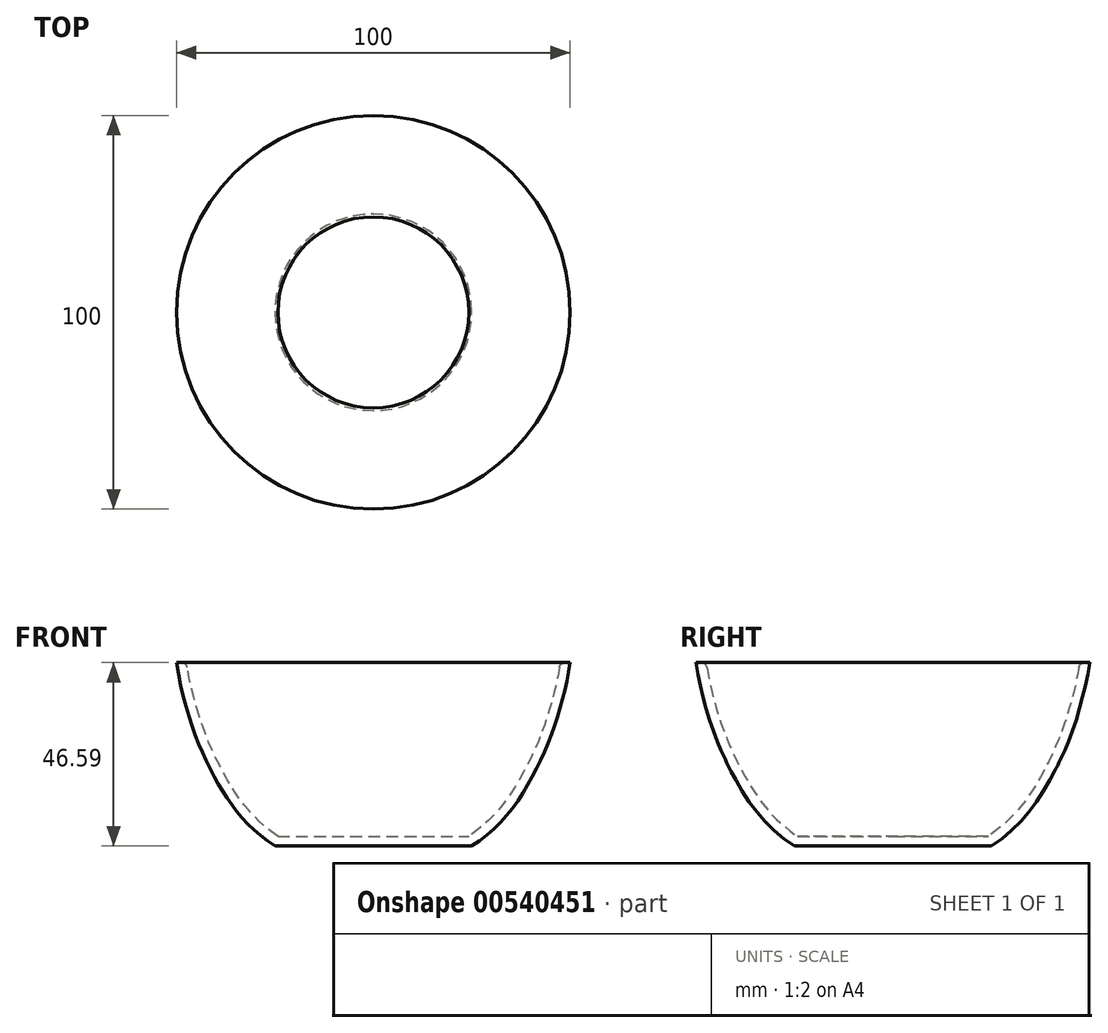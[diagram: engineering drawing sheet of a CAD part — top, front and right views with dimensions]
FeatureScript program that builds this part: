
annotation { "Feature Type Name" : "Feature", "Feature Type Description" : "" }
export const myFeature = defineFeature(function(context is Context, id is Id, definition is map)
    precondition{}
    {
        {
            var Q0;
            Q0=qCreatedBy(makeId("Front.planeOp"),FACE);
            var sketch = newSketch(context, id + "F0", { "sketchPlane" : qUnion([Q0])});
            skLineSegment(sketch, "E0", {"start": v(0, 0) * mm, "end": v(-25, 0) * mm});
            skLineSegment(sketch, "E1", {"start": v(0, 46.6) * mm, "end": v(-50, 46.6) * mm});
            skFitSpline(sketch, "E2", {"points": [v(-25, 0) * mm, v(-39.96, 16.84) * mm, v(-50, 46.6) * mm], "startDerivative": vector(-45.81, 29.3) * mm, "endDerivative": vector(-11.08, 68.91) * mm});
            skLineSegment(sketch, "E3", {"start": v(0, 0) * mm, "end": v(0, 46.6) * mm});
            skSolve(sketch);
        }
        {
            var Q0;
            Q0=makeQuery(id+"F0.imprint","IMPRINT",FACE,{"disambiguationData":[TD([[makeQuery(id+"F0.imprint","IMPRINT",EDGE,{"derivedFrom":sQuery(id+"F0.wireOp",EDGE,"E0")}),-1.0]])]});
            var Q1;
            Q1=sQuery(id+"F0.wireOp",EDGE,"E3");
            revolve(context, id + "F1", {"entities" : qUnion([Q0]), "axis" : qUnion([Q1]), "revolveType" : RevolveType.FULL});
        }
        {
            var Q0;
            Q0=makeQuery(id+"F1.opRevolve","SWEPT_FACE",FACE,{"disambiguationData":[OSD([sQuery(id+"F0.wireOp",EDGE,"E1")])]});
            shell(context, id + "F2", {"entities" : qUnion([Q0]), "thickness" : 2.5 * mm});
        }
        {
            var Q0;
            Q0=makeQuery(id+"F2.opShell","OFFSET_EDGE",EDGE,{"disambiguationData":[OSD([sQuery(id+"F0.wireOp",EDGE,"E1"),sQuery(id+"F0.wireOp",EDGE,"E2")])]});
            fillet(context, id + "F3", {"entities" : qUnion([Q0]), "radius" : 1.5 * mm, "tangentPropagation" : true, "allowEdgeOverflow" : false});
        }
    });
